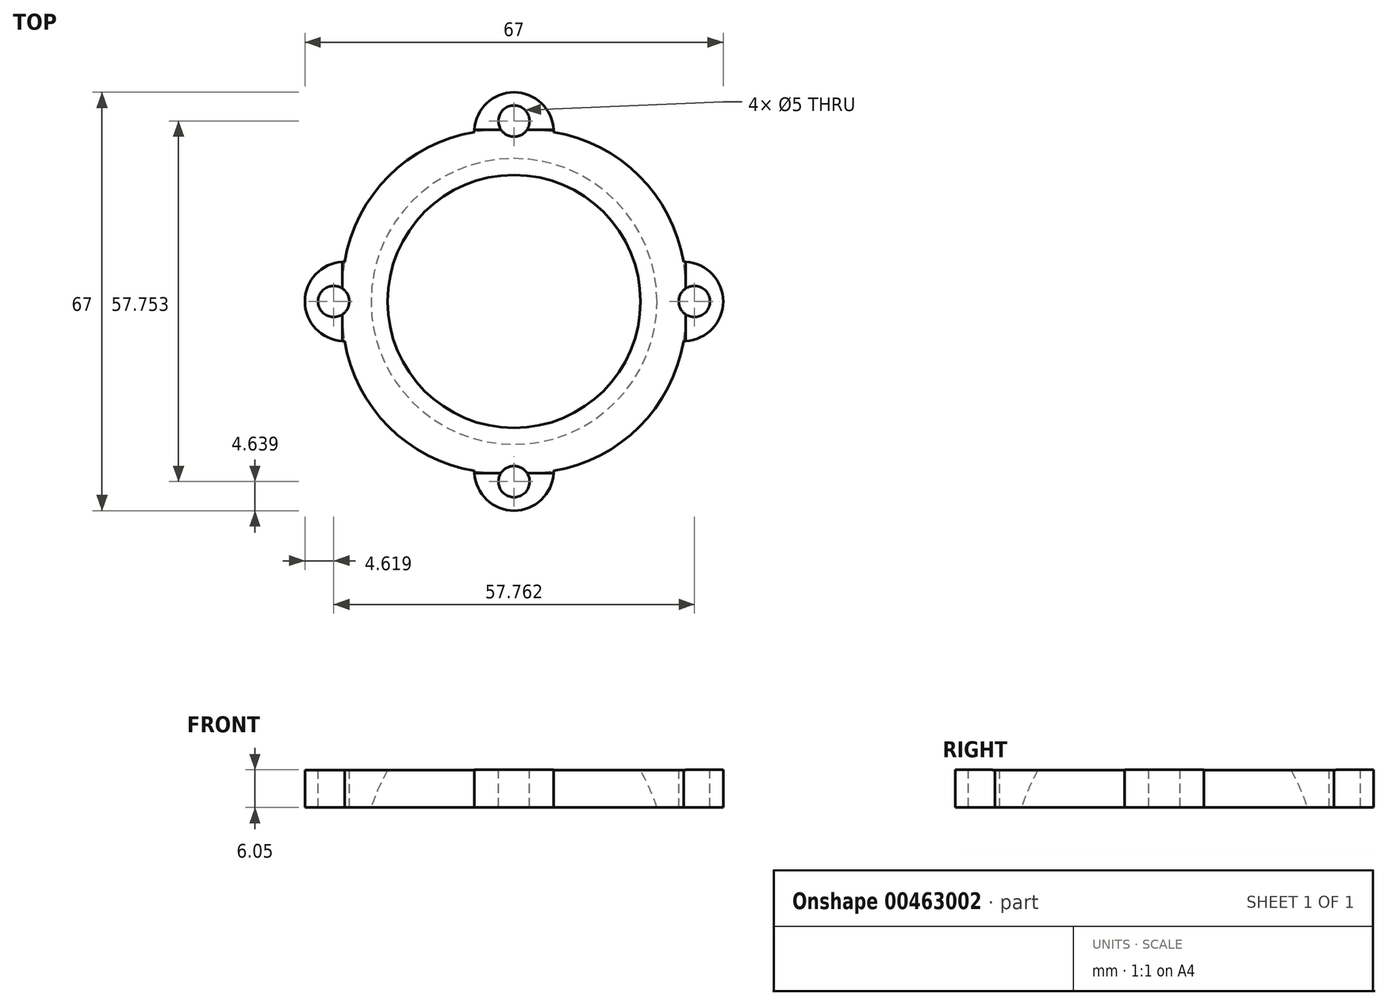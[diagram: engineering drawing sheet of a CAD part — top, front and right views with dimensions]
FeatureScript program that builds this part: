
annotation { "Feature Type Name" : "Feature", "Feature Type Description" : "" }
export const myFeature = defineFeature(function(context is Context, id is Id, definition is map)
    precondition{}
    {
        {
            var Q0;
            Q0=qCreatedBy(makeId("Front.planeOp"),FACE);
            var sketch = newSketch(context, id + "F0", { "sketchPlane" : qUnion([Q0])});
            skEllipticalArc(sketch, "E0", {});
            skLineSegment(sketch, "E1", {"start": v(0, 0) * mm, "end": v(0, 32.5) * mm});
            skLineSegment(sketch, "E2", {"start": v(0, 32.5) * mm, "end": v(0, -32.5) * mm});
            skLineSegment(sketch, "E3", {"start": v(0, 0) * mm, "end": v(25, 0) * mm});
            const initialGuessF0  = {"E0": [0, 0, 0, -1, 0.0325, 0.025, 0, 3.141592653589793]};
            skSetInitialGuess(sketch, initialGuessF0);
            skSolve(sketch);
        }
        {
            var Q0;
            {var subQ0=sQuery(id+"F0.wireOp",EDGE,"E0");Q0=makeQuery(id+"F0.imprint","IMPRINT",FACE,{"disambiguationData":[TD([[makeQuery(id+"F0.imprint","IMPRINT",EDGE,{"derivedFrom":subQ0}),1.0]])]});}
            var Q1;
            Q1=sQuery(id+"F0.wireOp",EDGE,"E2");
            revolve(context, id + "F1", {"entities" : qUnion([Q0]), "axis" : qUnion([Q1]), "revolveType" : RevolveType.FULL});
        }
        {
            var Q0;
            Q0=qCreatedBy(makeId("Top.planeOp"),FACE);
            cPlane(context, id + "F2", {"entities" : qUnion([Q0]), "cplaneType" : CPlaneType.OFFSET, "offset" : 19.05 * mm, "width" : 152.4 * mm, "height" : 152.4 * mm});
        }
        {
            var Q0;
            Q0=qCreatedBy(id+"F2.planeOp",FACE);
            var sketch = newSketch(context, id + "F3", { "sketchPlane" : qUnion([Q0])});
            skLineSegment(sketch, "E4.bottom", {"start": v(27.5, -27.5) * mm, "end": v(-27.5, -27.5) * mm});
            skLineSegment(sketch, "E4.top", {"start": v(27.5, 27.5) * mm, "end": v(-27.5, 27.5) * mm});
            skLineSegment(sketch, "E4.left", {"start": v(27.5, -27.5) * mm, "end": v(27.5, 27.5) * mm});
            skLineSegment(sketch, "E4.right", {"start": v(-27.5, -27.5) * mm, "end": v(-27.5, 27.5) * mm});
            skPoint(sketch, "E4.middle", {"position": v(0, 0) * mm});
            skSolve(sketch);
        }
        {
            var Q0;
            Q0 = qSketchRegion(id + "F3", true);
            extrude(context, id + "F4", {"entities" : qUnion([Q0]), "oppositeDirection" : true, "depth" : 6 * mm});
        }
        {
            var Q0;
            Q0=makeQuery(id+"F1.opRevolve","SWEPT_BODY",BODY,{"disambiguationData":[OSD([sQuery(id+"F0.wireOp",EDGE,"E0"),sQuery(id+"F0.wireOp",EDGE,"E2")])]});
            var Q1;
            Q1=makeQuery(id+"F4.opExtrude","SWEPT_BODY",BODY,{"disambiguationData":[OSD([sQuery(id+"F3.wireOp",EDGE,"E4.bottom"),sQuery(id+"F3.wireOp",EDGE,"E4.top"),sQuery(id+"F3.wireOp",EDGE,"E4.left"),sQuery(id+"F3.wireOp",EDGE,"E4.right")])]});
            booleanBodies(context, id + "F5", {"operationType" : BooleanOperationType.SUBTRACTION, "tools" : qUnion([Q0]), "targets" : qUnion([Q1])});
        }
        {
            var Q0;
            Q0=qCreatedBy(makeId("Front.planeOp"),FACE);
            var Q1;
            Q1 = qBodyType(qCreatedBy(id + "F7" ,EDGE), BodyType.WIRE);
            cPlane(context, id + "F6", {"entities" : qUnion([Q0, Q1]), "cplaneType" : CPlaneType.OFFSET, "offset" : 27.5 * mm, "width" : 152.4 * mm, "height" : 152.4 * mm});
        }
        {
            var Q0;
            Q0=qCreatedBy(id+"F6.planeOp",FACE);
            var sketch = newSketch(context, id + "F7", { "sketchPlane" : qUnion([Q0])});
            skLineSegment(sketch, "E5.bottom", {"start": v(6.35, 13.1) * mm, "end": v(-6.35, 13.1) * mm});
            skLineSegment(sketch, "E5.top", {"start": v(6.35, 19.1) * mm, "end": v(-6.35, 19.1) * mm});
            skLineSegment(sketch, "E5.left", {"start": v(6.35, 13.1) * mm, "end": v(6.35, 19.1) * mm});
            skLineSegment(sketch, "E5.right", {"start": v(-6.35, 13.1) * mm, "end": v(-6.35, 19.1) * mm});
            skPoint(sketch, "E5.middle", {"position": v(0, 16.1) * mm});
            skSolve(sketch);
        }
        {
            var Q0;
            Q0=makeQuery(id+"F7.imprint","IMPRINT",FACE,{"disambiguationData":[TD([[makeQuery(id+"F7.imprint","IMPRINT",EDGE,{"derivedFrom":sQuery(id+"F7.wireOp",EDGE,"E5.bottom")}),-1.0]])]});
            extrude(context, id + "F8", {"entities" : qUnion([Q0]), "operationType" : NewBodyOperationType.ADD, "depth" : 6 * mm});
        }
        {
            var Q0;
            Q0=qCreatedBy(makeId("Right.planeOp"),FACE);
            cPlane(context, id + "F9", {"entities" : qUnion([Q0]), "cplaneType" : CPlaneType.OFFSET, "offset" : 27.5 * mm, "width" : 152.4 * mm, "height" : 152.4 * mm});
        }
        {
            var Q0;
            Q0=qCreatedBy(id+"F9.planeOp",FACE);
            var sketch = newSketch(context, id + "F10", { "sketchPlane" : qUnion([Q0])});
            skLineSegment(sketch, "E6.bottom", {"start": v(6.35, 13.09) * mm, "end": v(-6.35, 13.09) * mm});
            skLineSegment(sketch, "E6.top", {"start": v(6.35, 19.09) * mm, "end": v(-6.35, 19.09) * mm});
            skLineSegment(sketch, "E6.left", {"start": v(6.35, 13.09) * mm, "end": v(6.35, 19.09) * mm});
            skLineSegment(sketch, "E6.right", {"start": v(-6.35, 13.09) * mm, "end": v(-6.35, 19.09) * mm});
            skPoint(sketch, "E6.middle", {"position": v(0, 16.09) * mm});
            skSolve(sketch);
        }
        {
            var Q0;
            Q0=makeQuery(id+"F10.imprint","IMPRINT",FACE,{"disambiguationData":[TD([[makeQuery(id+"F10.imprint","IMPRINT",EDGE,{"derivedFrom":sQuery(id+"F10.wireOp",EDGE,"E6.bottom")}),-1.0]])]});
            extrude(context, id + "F11", {"entities" : qUnion([Q0]), "operationType" : NewBodyOperationType.ADD, "depth" : 6 * mm});
        }
        {
            var Q0;
            Q0=qCreatedBy(makeId("Front.planeOp"),FACE);
            cPlane(context, id + "F12", {"entities" : qUnion([Q0]), "cplaneType" : CPlaneType.OFFSET, "offset" : 27.5 * mm, "oppositeDirection" : true, "width" : 152.4 * mm, "height" : 152.4 * mm});
        }
        {
            var Q0;
            Q0=qCreatedBy(id+"F12.planeOp",FACE);
            var sketch = newSketch(context, id + "F13", { "sketchPlane" : qUnion([Q0])});
            skLineSegment(sketch, "E7.bottom", {"start": v(6.35, 13.08) * mm, "end": v(-6.35, 13.08) * mm});
            skLineSegment(sketch, "E7.top", {"start": v(6.35, 19.08) * mm, "end": v(-6.35, 19.08) * mm});
            skLineSegment(sketch, "E7.left", {"start": v(6.35, 13.08) * mm, "end": v(6.35, 19.08) * mm});
            skLineSegment(sketch, "E7.right", {"start": v(-6.35, 13.08) * mm, "end": v(-6.35, 19.08) * mm});
            skPoint(sketch, "E7.middle", {"position": v(0, 16.08) * mm});
            skSolve(sketch);
        }
        {
            var Q0;
            Q0=makeQuery(id+"F13.imprint","IMPRINT",FACE,{"disambiguationData":[TD([[makeQuery(id+"F13.imprint","IMPRINT",EDGE,{"derivedFrom":sQuery(id+"F13.wireOp",EDGE,"E7.bottom")}),-1.0]])]});
            extrude(context, id + "F14", {"entities" : qUnion([Q0]), "operationType" : NewBodyOperationType.ADD, "oppositeDirection" : true, "depth" : 6 * mm});
        }
        {
            var Q0;
            Q0=qCreatedBy(makeId("Right.planeOp"),FACE);
            cPlane(context, id + "F15", {"entities" : qUnion([Q0]), "cplaneType" : CPlaneType.OFFSET, "offset" : 27.5 * mm, "oppositeDirection" : true, "width" : 152.4 * mm, "height" : 152.4 * mm});
        }
        {
            var Q0;
            Q0=qCreatedBy(id+"F15.planeOp",FACE);
            var sketch = newSketch(context, id + "F16", { "sketchPlane" : qUnion([Q0])});
            skLineSegment(sketch, "E8.bottom", {"start": v(-6.35, 13.06) * mm, "end": v(6.35, 13.06) * mm});
            skLineSegment(sketch, "E8.top", {"start": v(-6.35, 19.06) * mm, "end": v(6.35, 19.06) * mm});
            skLineSegment(sketch, "E8.left", {"start": v(-6.35, 13.06) * mm, "end": v(-6.35, 19.06) * mm});
            skLineSegment(sketch, "E8.right", {"start": v(6.35, 13.06) * mm, "end": v(6.35, 19.06) * mm});
            skPoint(sketch, "E8.middle", {"position": v(0, 16.06) * mm});
            skSolve(sketch);
        }
        {
            var Q0;
            Q0=makeQuery(id+"F16.imprint","IMPRINT",FACE,{"disambiguationData":[TD([[makeQuery(id+"F16.imprint","IMPRINT",EDGE,{"derivedFrom":sQuery(id+"F16.wireOp",EDGE,"E8.bottom")}),1.0]])]});
            extrude(context, id + "F17", {"entities" : qUnion([Q0]), "operationType" : NewBodyOperationType.ADD, "oppositeDirection" : true, "depth" : 6 * mm});
        }
        {
            var Q0;
            Q0=makeQuery(id+"F14.opExtrude","SWEPT_FACE",FACE,{"disambiguationData":[OSD([sQuery(id+"F13.wireOp",EDGE,"E7.top")])]});
            var sketch = newSketch(context, id + "F18", { "sketchPlane" : qUnion([Q0])});
            skLineSegment(sketch, "E9", {"start": v(0, 37.5) * mm, "end": v(0, 20.28) * mm});
            skPoint(sketch, "E9.endSnap0", {"position": v(0, 27.5) * mm});
            skPoint(sketch, "E10", {"position": v(0, 28.9) * mm});
            skSolve(sketch);
        }
        {
            var Q0;
            Q0=sQuery(id+"F18.wireOp",VERTEX,"E10");
            var Q1;
            Q1=makeQuery(id+"F4.opExtrude","SWEPT_BODY",BODY,{"disambiguationData":[OSD([sQuery(id+"F3.wireOp",EDGE,"E4.bottom"),sQuery(id+"F3.wireOp",EDGE,"E4.top"),sQuery(id+"F3.wireOp",EDGE,"E4.left"),sQuery(id+"F3.wireOp",EDGE,"E4.right")])]});
            hole(context, id + "F19", {"style" : HoleStyle.SIMPLE, "endStyle" : HoleEndStyle.THROUGH, "holeDiameter" : 5 * mm, "isTappedThrough" : true, "tappedDepth" : 12.7 * mm, "tapClearance" : 3, "locations" : qUnion([Q0]), "scope" : qUnion([Q1])});
        }
        {
            var Q0;
            Q0=makeQuery(id+"F17.opExtrude","SWEPT_FACE",FACE,{"disambiguationData":[OSD([sQuery(id+"F16.wireOp",EDGE,"E8.top")])]});
            var sketch = newSketch(context, id + "F20", { "sketchPlane" : qUnion([Q0])});
            skLineSegment(sketch, "E11", {"start": v(-37.5, 0) * mm, "end": v(-20.26, 0) * mm});
            skPoint(sketch, "E12", {"position": v(-28.88, 0) * mm});
            skSolve(sketch);
        }
        {
            var Q0;
            Q0=sQuery(id+"F20.wireOp",VERTEX,"E12");
            var Q1;
            Q1=makeQuery(id+"F4.opExtrude","SWEPT_BODY",BODY,{"disambiguationData":[OSD([sQuery(id+"F3.wireOp",EDGE,"E4.bottom"),sQuery(id+"F3.wireOp",EDGE,"E4.top"),sQuery(id+"F3.wireOp",EDGE,"E4.left"),sQuery(id+"F3.wireOp",EDGE,"E4.right")])]});
            hole(context, id + "F21", {"style" : HoleStyle.SIMPLE, "endStyle" : HoleEndStyle.THROUGH, "holeDiameter" : 5 * mm, "isTappedThrough" : true, "tappedDepth" : 12.7 * mm, "tapClearance" : 3, "locations" : qUnion([Q0]), "scope" : qUnion([Q1])});
        }
        {
            var Q0;
            Q0=makeQuery(id+"F11.opExtrude","SWEPT_FACE",FACE,{"disambiguationData":[OSD([sQuery(id+"F10.wireOp",EDGE,"E6.top")])]});
            var sketch = newSketch(context, id + "F22", { "sketchPlane" : qUnion([Q0])});
            skLineSegment(sketch, "E13", {"start": v(37.5, 0) * mm, "end": v(20.26, 0) * mm});
            skPoint(sketch, "E13.endSnap0", {"position": v(27.5, 0) * mm});
            skPoint(sketch, "E14", {"position": v(28.88, 0) * mm});
            skSolve(sketch);
        }
        {
            var Q0;
            Q0=sQuery(id+"F22.wireOp",VERTEX,"E14");
            var Q1;
            Q1=makeQuery(id+"F4.opExtrude","SWEPT_BODY",BODY,{"disambiguationData":[OSD([sQuery(id+"F3.wireOp",EDGE,"E4.bottom"),sQuery(id+"F3.wireOp",EDGE,"E4.top"),sQuery(id+"F3.wireOp",EDGE,"E4.left"),sQuery(id+"F3.wireOp",EDGE,"E4.right")])]});
            hole(context, id + "F23", {"style" : HoleStyle.SIMPLE, "endStyle" : HoleEndStyle.THROUGH, "holeDiameter" : 5 * mm, "isTappedThrough" : true, "tappedDepth" : 12.7 * mm, "tapClearance" : 3, "locations" : qUnion([Q0]), "scope" : qUnion([Q1])});
        }
        {
            var Q0;
            Q0=makeQuery(id+"F8.opExtrude","SWEPT_FACE",FACE,{"disambiguationData":[OSD([sQuery(id+"F7.wireOp",EDGE,"E5.top")])]});
            var sketch = newSketch(context, id + "F24", { "sketchPlane" : qUnion([Q0])});
            skLineSegment(sketch, "E15", {"start": v(0, -37.5) * mm, "end": v(0, -20.22) * mm});
            skPoint(sketch, "E15.endSnap0", {"position": v(0, -27.5) * mm});
            skPoint(sketch, "E16", {"position": v(0, -28.86) * mm});
            skSolve(sketch);
        }
        {
            var Q0;
            Q0=sQuery(id+"F24.wireOp",VERTEX,"E16");
            var Q1;
            Q1=makeQuery(id+"F4.opExtrude","SWEPT_BODY",BODY,{"disambiguationData":[OSD([sQuery(id+"F3.wireOp",EDGE,"E4.bottom"),sQuery(id+"F3.wireOp",EDGE,"E4.top"),sQuery(id+"F3.wireOp",EDGE,"E4.left"),sQuery(id+"F3.wireOp",EDGE,"E4.right")])]});
            hole(context, id + "F25", {"style" : HoleStyle.SIMPLE, "endStyle" : HoleEndStyle.THROUGH, "holeDiameter" : 5 * mm, "isTappedThrough" : true, "tappedDepth" : 12.7 * mm, "tapClearance" : 3, "locations" : qUnion([Q0]), "scope" : qUnion([Q1])});
        }
        {
            var Q0;
            Q0=makeQuery(id+"F4.opExtrude","SWEPT_EDGE",EDGE,{"disambiguationData":[OSD([sQuery(id+"F3.wireOp",EDGE,"E4.top"),sQuery(id+"F3.wireOp",EDGE,"E4.right")])]});
            var Q1;
            Q1=makeQuery(id+"F4.opExtrude","SWEPT_EDGE",EDGE,{"disambiguationData":[OSD([sQuery(id+"F3.wireOp",EDGE,"E4.bottom"),sQuery(id+"F3.wireOp",EDGE,"E4.right")])]});
            var Q2;
            Q2=makeQuery(id+"F4.opExtrude","SWEPT_EDGE",EDGE,{"disambiguationData":[OSD([sQuery(id+"F3.wireOp",EDGE,"E4.bottom"),sQuery(id+"F3.wireOp",EDGE,"E4.left")])]});
            var Q3;
            Q3=makeQuery(id+"F4.opExtrude","SWEPT_EDGE",EDGE,{"disambiguationData":[OSD([sQuery(id+"F3.wireOp",EDGE,"E4.top"),sQuery(id+"F3.wireOp",EDGE,"E4.left")])]});
            fillet(context, id + "F26", {"entities" : qUnion([Q0, Q1, Q2, Q3]), "radius" : 25.4 * mm, "tangentPropagation" : true, "allowEdgeOverflow" : false});
        }
        {
            var Q0;
            Q0=makeQuery(id+"F14.opExtrude","CAP_EDGE",EDGE,{"disambiguationData":[OSD([sQuery(id+"F13.wireOp",EDGE,"E7.left")])],"isStart":false});
            var Q1;
            Q1=makeQuery(id+"F14.opExtrude","CAP_EDGE",EDGE,{"disambiguationData":[OSD([sQuery(id+"F13.wireOp",EDGE,"E7.right")])],"isStart":false});
            var Q2;
            Q2=makeQuery(id+"F17.opExtrude","CAP_EDGE",EDGE,{"disambiguationData":[OSD([sQuery(id+"F16.wireOp",EDGE,"E8.right")])],"isStart":false});
            var Q3;
            Q3=makeQuery(id+"F17.opExtrude","CAP_EDGE",EDGE,{"disambiguationData":[OSD([sQuery(id+"F16.wireOp",EDGE,"E8.left")])],"isStart":false});
            var Q4;
            Q4=makeQuery(id+"F8.opExtrude","CAP_EDGE",EDGE,{"disambiguationData":[OSD([sQuery(id+"F7.wireOp",EDGE,"E5.right")])],"isStart":false});
            var Q5;
            Q5=makeQuery(id+"F8.opExtrude","CAP_EDGE",EDGE,{"disambiguationData":[OSD([sQuery(id+"F7.wireOp",EDGE,"E5.left")])],"isStart":false});
            var Q6;
            Q6=makeQuery(id+"F11.opExtrude","CAP_EDGE",EDGE,{"disambiguationData":[OSD([sQuery(id+"F10.wireOp",EDGE,"E6.right")])],"isStart":false});
            var Q7;
            Q7=makeQuery(id+"F11.opExtrude","CAP_EDGE",EDGE,{"disambiguationData":[OSD([sQuery(id+"F10.wireOp",EDGE,"E6.left")])],"isStart":false});
            fillet(context, id + "F27", {"entities" : qUnion([Q0, Q1, Q2, Q3, Q4, Q5, Q6, Q7]), "radius" : 6.35 * mm, "tangentPropagation" : true, "allowEdgeOverflow" : false});
        }
    });
